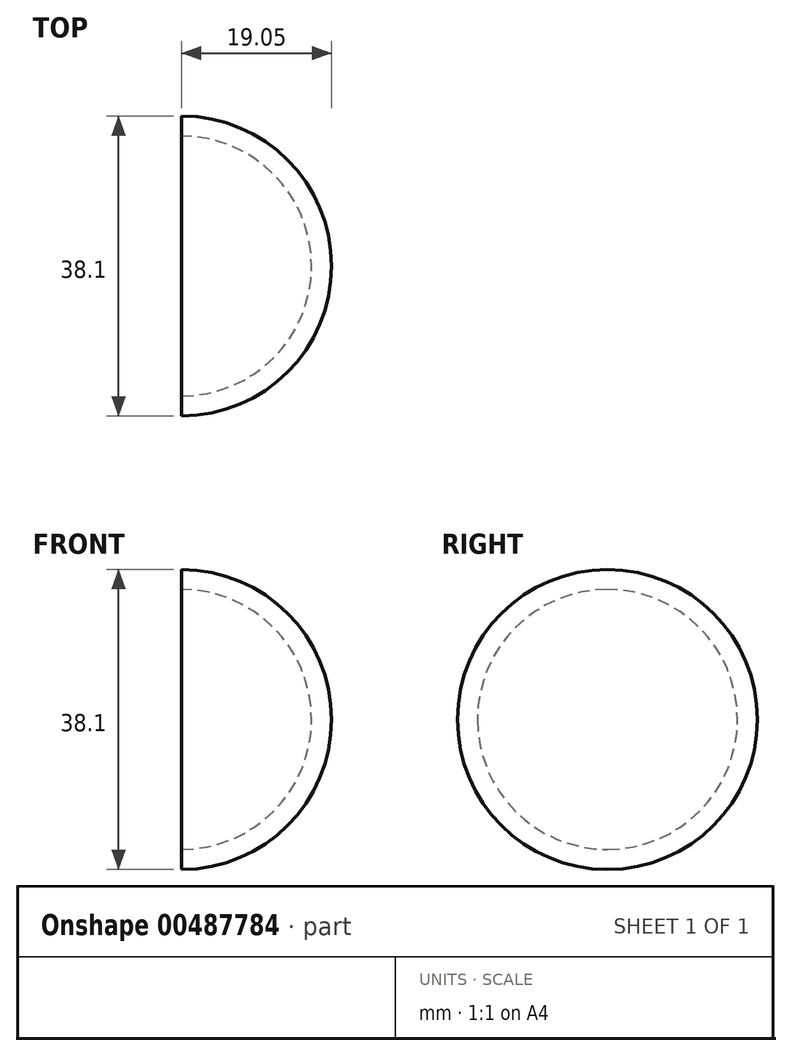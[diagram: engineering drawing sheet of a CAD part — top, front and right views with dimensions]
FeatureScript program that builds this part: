
annotation { "Feature Type Name" : "Feature", "Feature Type Description" : "" }
export const myFeature = defineFeature(function(context is Context, id is Id, definition is map)
    precondition{}
    {
        {
            var Q0;
            Q0=qCreatedBy(makeId("Front.planeOp"),FACE);
            var sketch = newSketch(context, id + "F0", { "sketchPlane" : qUnion([Q0])});
            skArc(sketch, "E0", {"start": v(0, -19.05) * mm, "mid": v(19.05, 0) * mm, "end": v(0, 19.05) * mm});
            skPoint(sketch, "E1.orphan", {"position": v(0, -19.05) * mm});
            skLineSegment(sketch, "E2", {"start": v(0, 19.05) * mm, "end": v(0, -19.05) * mm});
            skSolve(sketch);
        }
        {
            var Q0;
            Q0 = qSketchRegion(id + "F0", true);
            var Q1;
            Q1=sQuery(id+"F0.wireOp",EDGE,"E2");
            revolve(context, id + "F1", {"entities" : qUnion([Q0]), "axis" : qUnion([Q1]), "revolveType" : RevolveType.SYMMETRIC, "angle" : 180 * degree});
        }
        {
            var Q0;
            Q0=makeQuery(id+"F1.opRevolve","CAP_FACE",FACE,{"disambiguationData":[OSD([sQuery(id+"F0.wireOp",EDGE,"E0"),sQuery(id+"F0.wireOp",EDGE,"E2")])],"isStart":true});
            shell(context, id + "F2", {"entities" : qUnion([Q0]), "thickness" : 2.54 * mm});
        }
    });
